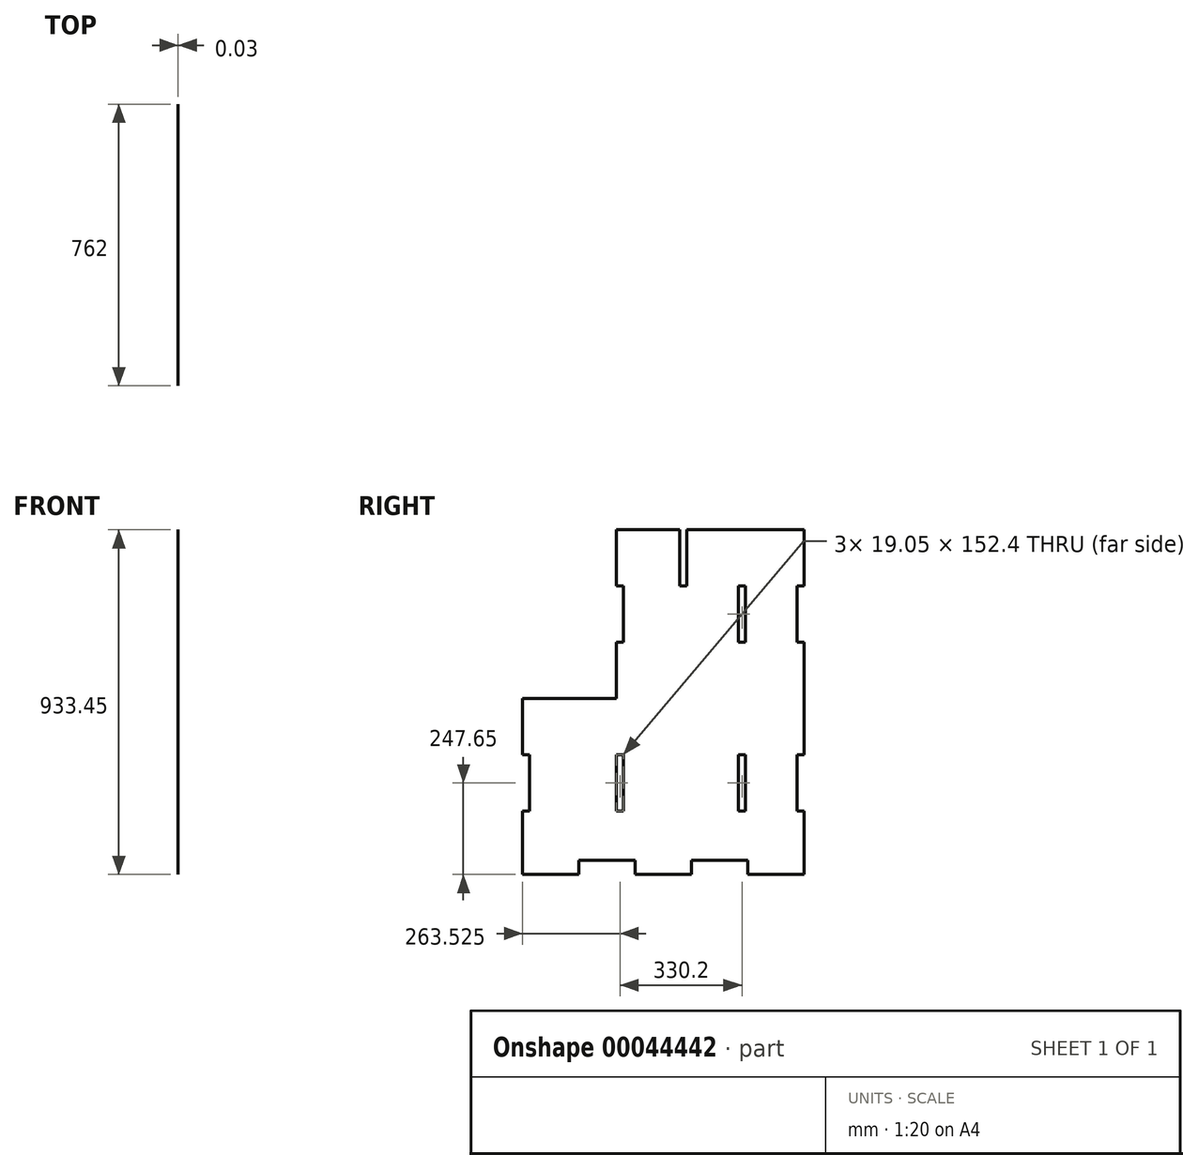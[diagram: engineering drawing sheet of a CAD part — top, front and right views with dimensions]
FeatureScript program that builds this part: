
annotation { "Feature Type Name" : "Feature", "Feature Type Description" : "" }
export const myFeature = defineFeature(function(context is Context, id is Id, definition is map)
    precondition{}
    {
        {
            var Q0;
            Q0=qCreatedBy(makeId("Right.planeOp"),FACE);
            var sketch = newSketch(context, id + "F0", { "sketchPlane" : qUnion([Q0])});
            skLineSegment(sketch, "E0", {"start": v(-381, 50.8) * mm, "end": v(-381, -425.45) * mm});
            skLineSegment(sketch, "E1", {"start": v(-381, -425.45) * mm, "end": v(381, -425.45) * mm});
            skLineSegment(sketch, "E2", {"start": v(381, -425.45) * mm, "end": v(381, 508) * mm});
            skLineSegment(sketch, "E3", {"start": v(381, 508) * mm, "end": v(-127, 508) * mm});
            skLineSegment(sketch, "E4", {"start": v(-127, 508) * mm, "end": v(-127, 50.8) * mm});
            skLineSegment(sketch, "E5", {"start": v(-127, 50.8) * mm, "end": v(-381, 50.8) * mm});
            skSolve(sketch);
        }
        {
            var Q0;
            Q0 = qSketchRegion(id + "F0", true);
            extrude(context, id + "F1", {"entities" : qUnion([Q0]), "depth" : 3 / 101.6 * mm});
        }
        {
            var Q0;
            Q0=makeQuery(id+"F1.opExtrude","CAP_FACE",FACE,{"disambiguationData":[OSD([sQuery(id+"F0.wireOp",EDGE,"E0"),sQuery(id+"F0.wireOp",EDGE,"E1"),sQuery(id+"F0.wireOp",EDGE,"E2"),sQuery(id+"F0.wireOp",EDGE,"E3"),sQuery(id+"F0.wireOp",EDGE,"E4"),sQuery(id+"F0.wireOp",EDGE,"E5")])],"isStart":false});
            var sketch = newSketch(context, id + "F2", { "sketchPlane" : qUnion([Q0])});
            skLineSegment(sketch, "E6.bottom", {"start": v(381, 355.6) * mm, "end": v(361.95, 355.6) * mm});
            skLineSegment(sketch, "E6.top", {"start": v(381, 203.2) * mm, "end": v(361.95, 203.2) * mm});
            skLineSegment(sketch, "E6.left", {"start": v(381, 355.6) * mm, "end": v(381, 203.2) * mm});
            skLineSegment(sketch, "E6.right", {"start": v(361.95, 355.6) * mm, "end": v(361.95, 203.2) * mm});
            skLineSegment(sketch, "E7.bottom", {"start": v(381, -101.6) * mm, "end": v(361.95, -101.6) * mm});
            skLineSegment(sketch, "E7.top", {"start": v(381, -254) * mm, "end": v(361.95, -254) * mm});
            skLineSegment(sketch, "E7.left", {"start": v(381, -101.6) * mm, "end": v(381, -254) * mm});
            skLineSegment(sketch, "E7.right", {"start": v(361.95, -101.6) * mm, "end": v(361.95, -254) * mm});
            skLineSegment(sketch, "E8.bottom", {"start": v(44.45, 508) * mm, "end": v(63.5, 508) * mm});
            skLineSegment(sketch, "E8.top", {"start": v(44.45, 355.6) * mm, "end": v(63.5, 355.6) * mm});
            skLineSegment(sketch, "E8.left", {"start": v(44.45, 508) * mm, "end": v(44.45, 355.6) * mm});
            skLineSegment(sketch, "E8.right", {"start": v(63.5, 508) * mm, "end": v(63.5, 355.6) * mm});
            skLineSegment(sketch, "E9.bottom", {"start": v(-127, 355.6) * mm, "end": v(-107.95, 355.6) * mm});
            skLineSegment(sketch, "E9.top", {"start": v(-127, 203.2) * mm, "end": v(-107.95, 203.2) * mm});
            skLineSegment(sketch, "E9.left", {"start": v(-127, 355.6) * mm, "end": v(-127, 203.2) * mm});
            skLineSegment(sketch, "E9.right", {"start": v(-107.95, 355.6) * mm, "end": v(-107.95, 203.2) * mm});
            skLineSegment(sketch, "E10.bottom", {"start": v(203.2, 355.6) * mm, "end": v(222.25, 355.6) * mm});
            skLineSegment(sketch, "E10.top", {"start": v(203.2, 203.2) * mm, "end": v(222.25, 203.2) * mm});
            skLineSegment(sketch, "E10.left", {"start": v(203.2, 355.6) * mm, "end": v(203.2, 203.2) * mm});
            skLineSegment(sketch, "E10.right", {"start": v(222.25, 355.6) * mm, "end": v(222.25, 203.2) * mm});
            skLineSegment(sketch, "E11.bottom", {"start": v(203.2, -101.6) * mm, "end": v(222.25, -101.6) * mm});
            skLineSegment(sketch, "E11.top", {"start": v(203.2, -254) * mm, "end": v(222.25, -254) * mm});
            skLineSegment(sketch, "E11.left", {"start": v(203.2, -101.6) * mm, "end": v(203.2, -254) * mm});
            skLineSegment(sketch, "E11.right", {"start": v(222.25, -101.6) * mm, "end": v(222.25, -254) * mm});
            skLineSegment(sketch, "E12.bottom", {"start": v(-127, -101.6) * mm, "end": v(-107.95, -101.6) * mm});
            skLineSegment(sketch, "E12.top", {"start": v(-127, -254) * mm, "end": v(-107.95, -254) * mm});
            skLineSegment(sketch, "E12.left", {"start": v(-127, -101.6) * mm, "end": v(-127, -254) * mm});
            skLineSegment(sketch, "E12.right", {"start": v(-107.95, -101.6) * mm, "end": v(-107.95, -254) * mm});
            skLineSegment(sketch, "E13.bottom", {"start": v(-381, -101.6) * mm, "end": v(-361.95, -101.6) * mm});
            skLineSegment(sketch, "E13.top", {"start": v(-381, -254) * mm, "end": v(-361.95, -254) * mm});
            skLineSegment(sketch, "E13.left", {"start": v(-381, -101.6) * mm, "end": v(-381, -254) * mm});
            skLineSegment(sketch, "E13.right", {"start": v(-361.95, -101.6) * mm, "end": v(-361.95, -254) * mm});
            skLineSegment(sketch, "E14.bottom", {"start": v(228.6, -425.45) * mm, "end": v(76.2, -425.45) * mm});
            skLineSegment(sketch, "E14.top", {"start": v(228.6, -387.35) * mm, "end": v(76.2, -387.35) * mm});
            skLineSegment(sketch, "E14.left", {"start": v(228.6, -425.45) * mm, "end": v(228.6, -387.35) * mm});
            skLineSegment(sketch, "E14.right", {"start": v(76.2, -425.45) * mm, "end": v(76.2, -387.35) * mm});
            skLineSegment(sketch, "E15.bottom", {"start": v(-76.2, -425.45) * mm, "end": v(-228.6, -425.45) * mm});
            skLineSegment(sketch, "E15.top", {"start": v(-76.2, -387.35) * mm, "end": v(-228.6, -387.35) * mm});
            skLineSegment(sketch, "E15.left", {"start": v(-76.2, -425.45) * mm, "end": v(-76.2, -387.35) * mm});
            skLineSegment(sketch, "E15.right", {"start": v(-228.6, -425.45) * mm, "end": v(-228.6, -387.35) * mm});
            skSolve(sketch);
        }
        {
            var Q0;
            Q0 = qSketchRegion(id + "F2", true);
            extrude(context, id + "F3", {"entities" : qUnion([Q0]), "operationType" : NewBodyOperationType.REMOVE, "oppositeDirection" : true, "depth" : 19.05 * mm});
        }
    });
